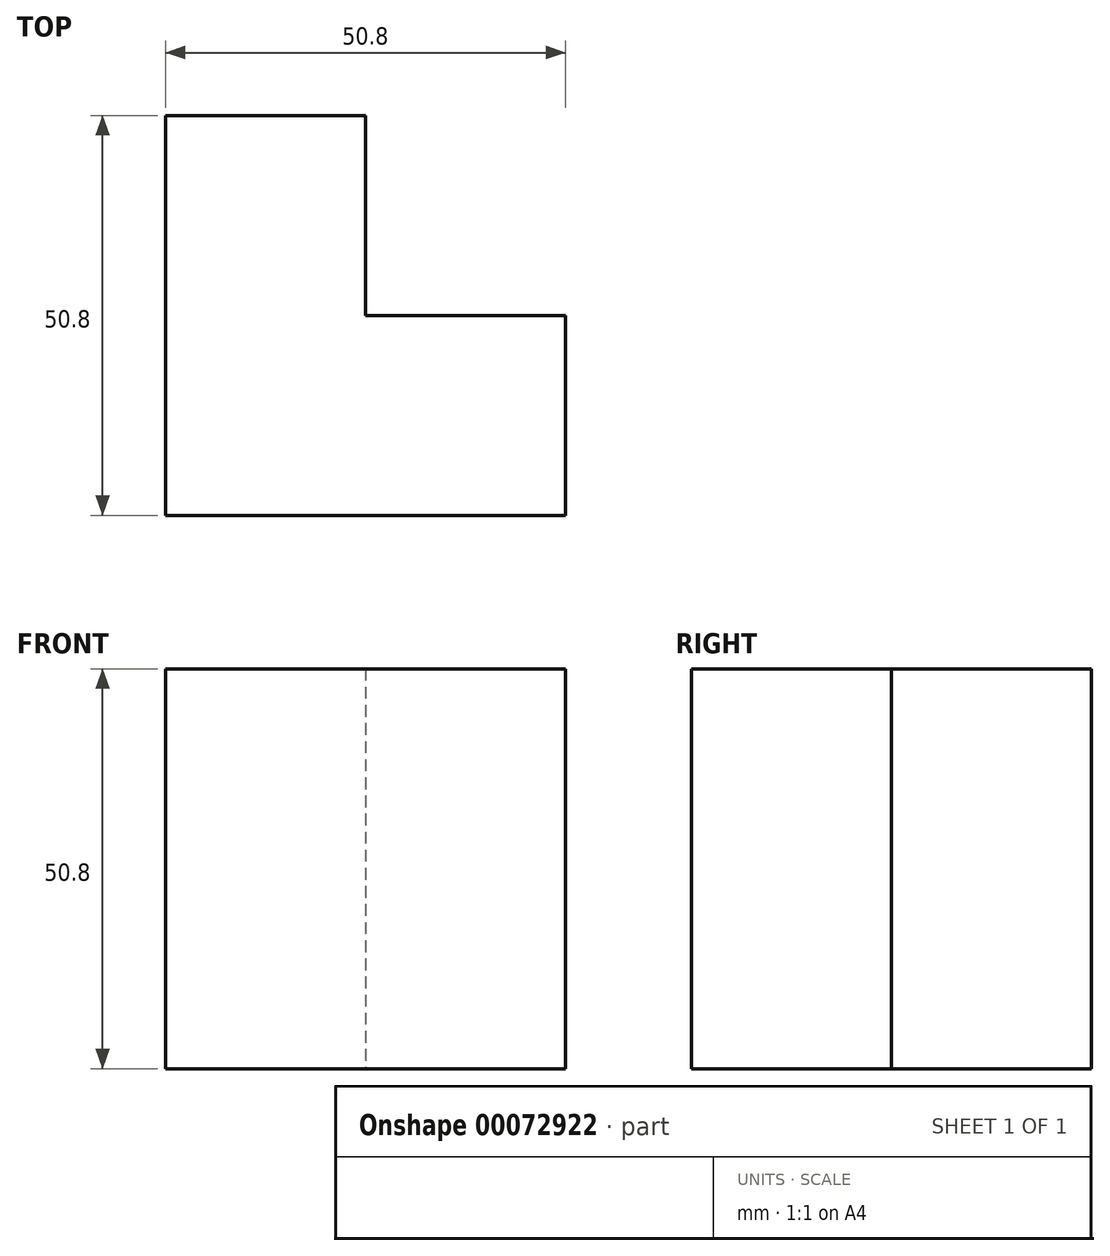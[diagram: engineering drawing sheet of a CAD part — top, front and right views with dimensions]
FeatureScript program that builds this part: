
annotation { "Feature Type Name" : "Feature", "Feature Type Description" : "" }
export const myFeature = defineFeature(function(context is Context, id is Id, definition is map)
    precondition{}
    {
        {
            var Q0;
            Q0=qCreatedBy(makeId("Top.planeOp"),FACE);
            var sketch = newSketch(context, id + "F0", { "sketchPlane" : qUnion([Q0])});
            skLineSegment(sketch, "E0", {"start": v(-47.13, 37.4) * mm, "end": v(-47.13, -13.4) * mm});
            skLineSegment(sketch, "E1", {"start": v(-47.13, -13.4) * mm, "end": v(3.67, -13.4) * mm});
            skLineSegment(sketch, "E2", {"start": v(3.67, -13.4) * mm, "end": v(3.67, 12) * mm});
            skLineSegment(sketch, "E3", {"start": v(3.67, 12) * mm, "end": v(-21.73, 12) * mm});
            skLineSegment(sketch, "E4", {"start": v(-21.73, 12) * mm, "end": v(-21.73, 37.4) * mm});
            skLineSegment(sketch, "E5", {"start": v(-21.73, 37.4) * mm, "end": v(-47.13, 37.4) * mm});
            skSolve(sketch);
        }
        {
            var Q0;
            Q0 = qSketchRegion(id + "F0", true);
            extrude(context, id + "F1", {"entities" : qUnion([Q0]), "depth" : 50.8 * mm});
        }
    });
